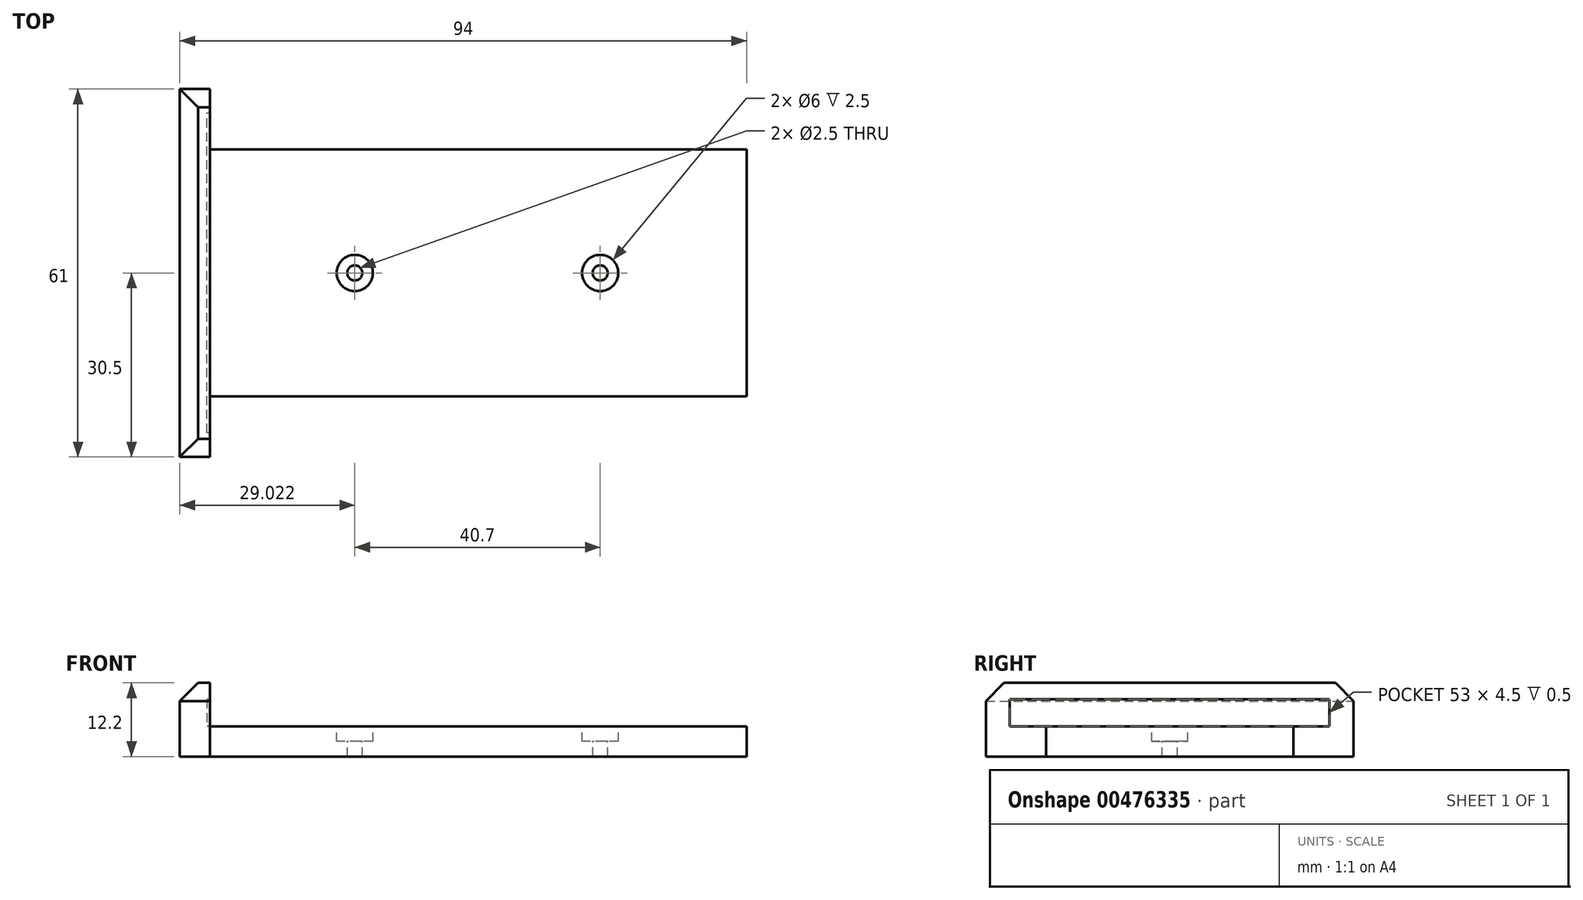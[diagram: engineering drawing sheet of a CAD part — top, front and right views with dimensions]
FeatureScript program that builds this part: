
annotation { "Feature Type Name" : "Feature", "Feature Type Description" : "" }
export const myFeature = defineFeature(function(context is Context, id is Id, definition is map)
    precondition{}
    {
        {
            var Q0;
            Q0=qCreatedBy(makeId("Top.planeOp"),FACE);
            var sketch = newSketch(context, id + "F0", { "sketchPlane" : qUnion([Q0])});
            skLineSegment(sketch, "E0.rect.bottom", {"start": v(44.5, -20.5) * mm, "end": v(-44.5, -20.5) * mm});
            skLineSegment(sketch, "E0.rect.top", {"start": v(44.5, 20.5) * mm, "end": v(-44.5, 20.5) * mm});
            skLineSegment(sketch, "E0.rect.left", {"start": v(44.5, -20.5) * mm, "end": v(44.5, 20.5) * mm});
            skLineSegment(sketch, "E0.rect.right", {"start": v(-44.5, -20.5) * mm, "end": v(-44.5, 20.5) * mm});
            skPoint(sketch, "E0.rect.middle", {"position": v(0, 0) * mm});
            skLineSegment(sketch, "E1.bottom", {"start": v(-44.5, 20.5) * mm, "end": v(44.5, 20.5) * mm});
            skLineSegment(sketch, "E1.top", {"start": v(-44.5, 30.5) * mm, "end": v(44.5, 30.5) * mm});
            skLineSegment(sketch, "E1.left", {"start": v(-44.5, 20.5) * mm, "end": v(-44.5, 30.5) * mm});
            skLineSegment(sketch, "E1.right", {"start": v(44.5, 20.5) * mm, "end": v(44.5, 30.5) * mm});
            skLineSegment(sketch, "E2.bottom", {"start": v(-44.5, -20.5) * mm, "end": v(44.5, -20.5) * mm});
            skLineSegment(sketch, "E2.top", {"start": v(-44.5, -30.5) * mm, "end": v(44.5, -30.5) * mm});
            skLineSegment(sketch, "E2.left", {"start": v(-44.5, -20.5) * mm, "end": v(-44.5, -30.5) * mm});
            skLineSegment(sketch, "E2.right", {"start": v(44.5, -20.5) * mm, "end": v(44.5, -30.5) * mm});
            skLineSegment(sketch, "E3.bottom", {"start": v(-44.5, 30.5) * mm, "end": v(-49.5, 30.5) * mm});
            skLineSegment(sketch, "E3.top", {"start": v(-44.5, -30.5) * mm, "end": v(-49.5, -30.5) * mm});
            skLineSegment(sketch, "E3.left", {"start": v(-44.5, 30.5) * mm, "end": v(-44.5, -30.5) * mm});
            skLineSegment(sketch, "E3.right", {"start": v(-49.5, 30.5) * mm, "end": v(-49.5, -30.5) * mm});
            skSolve(sketch);
        }
        {
            var Q0;
            Q0=makeQuery(id+"F0.imprint","IMPRINT",FACE,{"disambiguationData":[TD([[makeQuery(id+"F0.imprint","IMPRINT",EDGE,{"derivedFrom":sQuery(id+"F0.wireOp",EDGE,"E0.rect.left")}),1.0]])]});
            extrude(context, id + "F1", {"entities" : qUnion([Q0]), "depth" : 5 * mm});
        }
        {
            var Q0;
            {var subQ2=sQuery(id+"F0.wireOp",EDGE,"E2.bottom");Q0=makeQuery(id+"F0.imprint","IMPRINT",FACE,{"disambiguationData":[TD([[makeQuery(id+"F0.imprint","IMPRINT",EDGE,{"derivedFrom":subQ2}),-1.0]])]});}
            var Q1;
            {var subQ2=sQuery(id+"F0.wireOp",EDGE,"E1.bottom");Q1=makeQuery(id+"F0.imprint","IMPRINT",FACE,{"disambiguationData":[TD([[makeQuery(id+"F0.imprint","IMPRINT",EDGE,{"derivedFrom":subQ2}),1.0]])]});}
            var Q2;
            {var subQ4=sQuery(id+"F0.wireOp",EDGE,"E3.bottom");Q2=makeQuery(id+"F0.imprint","IMPRINT",FACE,{"disambiguationData":[TD([[makeQuery(id+"F0.imprint","IMPRINT",EDGE,{"derivedFrom":subQ4}),1.0]])]});}
            extrude(context, id + "F2", {"entities" : qUnion([Q0, Q1, Q2]), "operationType" : NewBodyOperationType.ADD, "depth" : 12.2 * mm});
        }
        {
            var Q0;
            Q0=makeQuery(id+"F1.opExtrude","CAP_FACE",FACE,{"disambiguationData":[OSD([sQuery(id+"F0.wireOp",EDGE,"E0.rect.left"),sQuery(id+"F0.wireOp",EDGE,"E1.bottom"),sQuery(id+"F0.wireOp",EDGE,"E2.bottom"),sQuery(id+"F0.wireOp",EDGE,"E3.left")])],"isStart":false});
            var sketch = newSketch(context, id + "F3", { "sketchPlane" : qUnion([Q0])});
            skLineSegment(sketch, "E4.rect.bottom", {"start": v(45, -26.5) * mm, "end": v(-45, -26.5) * mm});
            skLineSegment(sketch, "E4.rect.top", {"start": v(45, 26.5) * mm, "end": v(-45, 26.5) * mm});
            skLineSegment(sketch, "E4.rect.left", {"start": v(45, -26.5) * mm, "end": v(45, 26.5) * mm});
            skLineSegment(sketch, "E4.rect.right", {"start": v(-45, -26.5) * mm, "end": v(-45, 26.5) * mm});
            skPoint(sketch, "E4.rect.middle", {"position": v(0, 0) * mm});
            skSolve(sketch);
        }
        {
            var Q0;
            Q0=qSketchRegion(id+"F3",true);
            extrude(context, id + "F4", {"entities" : qUnion([Q0]), "operationType" : NewBodyOperationType.REMOVE, "depth" : 4.5 * mm});
        }
        {
            var Q0;
            Q0=makeQuery(id+"F2.opExtrude","CAP_EDGE",EDGE,{"disambiguationData":[OSD([sQuery(id+"F0.wireOp",EDGE,"E2.top"),sQuery(id+"F0.wireOp",EDGE,"E3.top")])],"isStart":false});
            var Q1;
            Q1=makeQuery(id+"F2.opExtrude","CAP_EDGE",EDGE,{"disambiguationData":[OSD([sQuery(id+"F0.wireOp",EDGE,"E3.right")])],"isStart":false});
            var Q2;
            Q2=makeQuery(id+"F2.opExtrude","CAP_EDGE",EDGE,{"disambiguationData":[OSD([sQuery(id+"F0.wireOp",EDGE,"E1.top"),sQuery(id+"F0.wireOp",EDGE,"E3.bottom")])],"isStart":false});
            chamfer(context, id + "F5", {"entities" : qUnion([Q0, Q1, Q2]), "width" : 3 * mm, "tangentPropagation" : true});
        }
        {
            var Q0;
            Q0=makeQuery(id+"F4.boolean.opBoolean","MERGE",FACE,{"derivedFrom":[makeQuery(id+"F1.opExtrude","CAP_FACE",FACE,{"disambiguationData":[OSD([sQuery(id+"F0.wireOp",EDGE,"E0.rect.left"),sQuery(id+"F0.wireOp",EDGE,"E1.bottom"),sQuery(id+"F0.wireOp",EDGE,"E2.bottom"),sQuery(id+"F0.wireOp",EDGE,"E3.left")])],"isStart":false}),makeQuery(id+"F4.opExtrude","CAP_FACE",FACE,{"disambiguationData":[OSD([sQuery(id+"F3.wireOp",EDGE,"E4.rect.bottom"),sQuery(id+"F3.wireOp",EDGE,"E4.rect.top"),sQuery(id+"F3.wireOp",EDGE,"E4.rect.left"),sQuery(id+"F3.wireOp",EDGE,"E4.rect.right")])],"isStart":true})]});
            var sketch = newSketch(context, id + "F6", { "sketchPlane" : qUnion([Q0])});
            skCircle(sketch, "E5", {"center": v(-20.48, 0) * mm, "radius": 3 * mm});
            skCircle(sketch, "E6", {"center": v(20.22, 0) * mm, "radius": 3 * mm});
            skCircle(sketch, "E7", {"center": v(-20.48, 0) * mm, "radius": 1.25 * mm});
            skCircle(sketch, "E8", {"center": v(20.22, 0) * mm, "radius": 1.25 * mm});
            skSolve(sketch);
        }
        {
            var Q0;
            Q0=makeQuery(id+"F6.imprint","IMPRINT",FACE,{"disambiguationData":[TD([[makeQuery(id+"F6.imprint","IMPRINT",EDGE,{"derivedFrom":sQuery(id+"F6.wireOp",EDGE,"E8")}),1.0]])]});
            var Q1;
            Q1=makeQuery(id+"F6.imprint","IMPRINT",FACE,{"disambiguationData":[TD([[makeQuery(id+"F6.imprint","IMPRINT",EDGE,{"derivedFrom":sQuery(id+"F6.wireOp",EDGE,"E6")}),1.0]])]});
            extrude(context, id + "F7", {"entities" : qUnion([Q0, Q1]), "operationType" : NewBodyOperationType.REMOVE, "oppositeDirection" : true, "depth" : 2.5 * mm});
        }
        {
            var Q0;
            Q0=makeQuery(id+"F6.imprint","IMPRINT",FACE,{"disambiguationData":[TD([[makeQuery(id+"F6.imprint","IMPRINT",EDGE,{"derivedFrom":sQuery(id+"F6.wireOp",EDGE,"E5")}),1.0]])]});
            var Q1;
            Q1=makeQuery(id+"F6.imprint","IMPRINT",FACE,{"disambiguationData":[TD([[makeQuery(id+"F6.imprint","IMPRINT",EDGE,{"derivedFrom":sQuery(id+"F6.wireOp",EDGE,"E7")}),1.0]])]});
            extrude(context, id + "F8", {"entities" : qUnion([Q0, Q1]), "operationType" : NewBodyOperationType.REMOVE, "oppositeDirection" : true, "depth" : 2.5 * mm});
        }
        {
            var Q0;
            Q0=makeQuery(id+"F6.imprint","IMPRINT",FACE,{"disambiguationData":[TD([[makeQuery(id+"F6.imprint","IMPRINT",EDGE,{"derivedFrom":sQuery(id+"F6.wireOp",EDGE,"E7")}),1.0]])]});
            var Q1;
            Q1=sQuery(id+"F6.wireOp",EDGE,"E7");
            extrude(context, id + "F9", {"entities" : qUnion([Q0]), "operationType" : NewBodyOperationType.REMOVE, "surfaceEntities" : qUnion([Q1]), "oppositeDirection" : true, "depth" : 25 * mm});
        }
        {
            var Q0;
            Q0=makeQuery(id+"F6.imprint","IMPRINT",FACE,{"disambiguationData":[TD([[makeQuery(id+"F6.imprint","IMPRINT",EDGE,{"derivedFrom":sQuery(id+"F6.wireOp",EDGE,"E8")}),1.0]])]});
            var Q1;
            Q1=sQuery(id+"F6.wireOp",EDGE,"E8");
            extrude(context, id + "F10", {"entities" : qUnion([Q0]), "operationType" : NewBodyOperationType.REMOVE, "surfaceEntities" : qUnion([Q1]), "oppositeDirection" : true, "depth" : 25 * mm});
        }
    });
